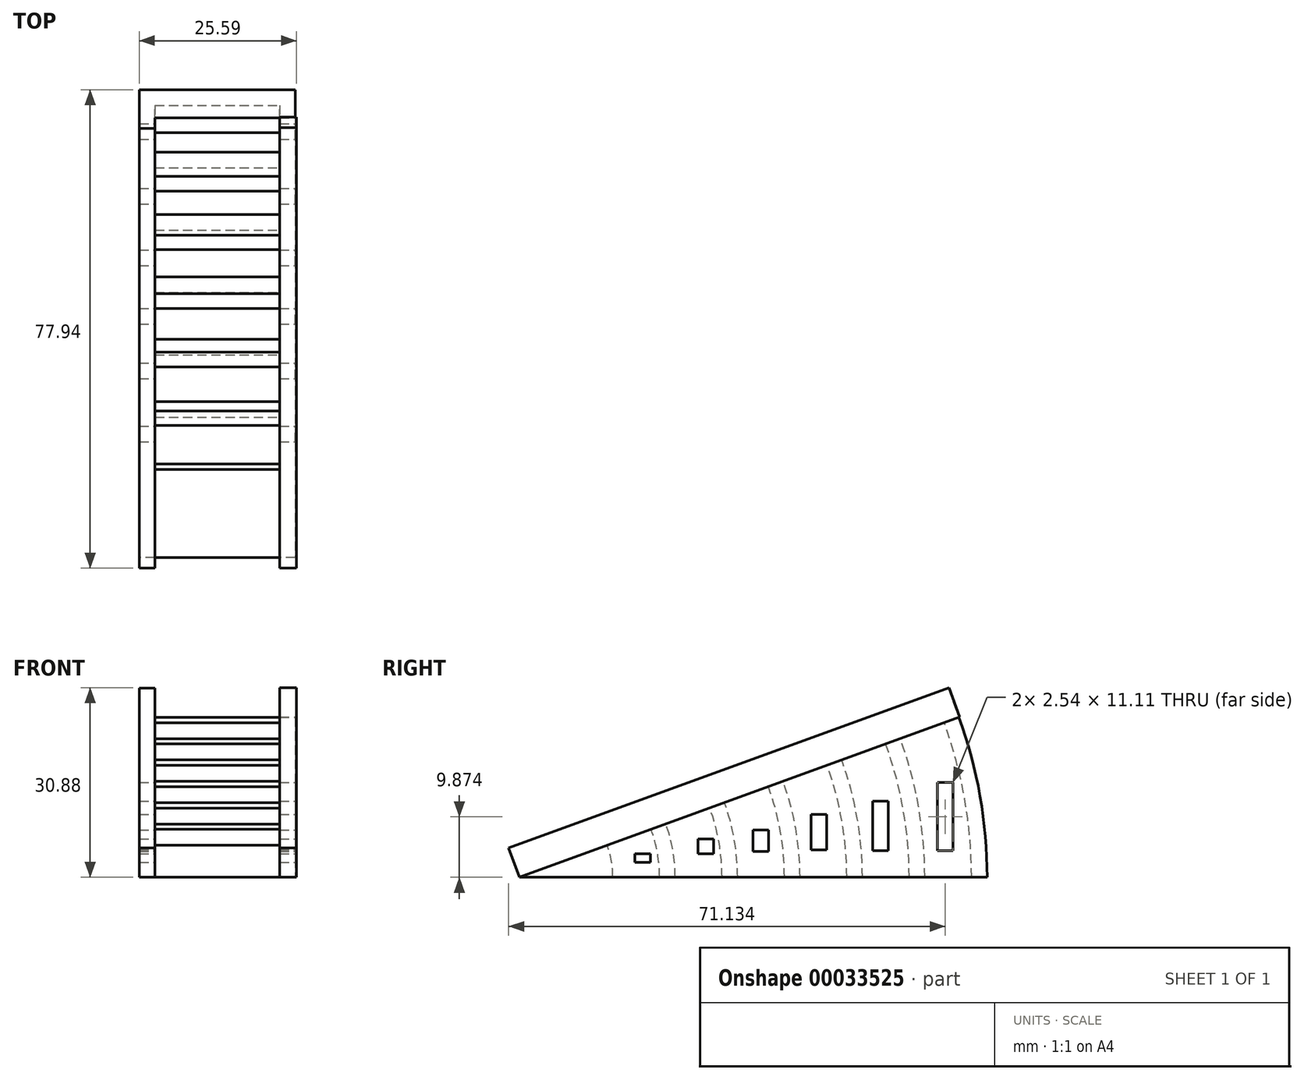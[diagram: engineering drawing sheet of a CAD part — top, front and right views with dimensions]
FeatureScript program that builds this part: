
annotation { "Feature Type Name" : "Feature", "Feature Type Description" : "" }
export const myFeature = defineFeature(function(context is Context, id is Id, definition is map)
    precondition{}
    {
        {
            var Q0;
            Q0=qCreatedBy(makeId("Top.planeOp"),FACE);
            var sketch = newSketch(context, id + "F0", { "sketchPlane" : qUnion([Q0])});
            skLineSegment(sketch, "E0", {"start": v(-12.56, 0) * mm, "end": v(-12.56, 76.2) * mm});
            skLineSegment(sketch, "E1", {"start": v(-12.56, 76.2) * mm, "end": v(12.84, 76.2) * mm});
            skLineSegment(sketch, "E2", {"start": v(12.84, 76.2) * mm, "end": v(12.84, 0) * mm});
            skLineSegment(sketch, "E3", {"start": v(12.84, 0) * mm, "end": v(-12.56, 0) * mm});
            skLineSegment(sketch, "E4.bottom", {"start": v(-10.02, 73.66) * mm, "end": v(10.3, 73.66) * mm});
            skLineSegment(sketch, "E4.top", {"start": v(-10.02, 66.04) * mm, "end": v(10.3, 66.04) * mm});
            skLineSegment(sketch, "E4.left", {"start": v(-10.02, 73.66) * mm, "end": v(-10.02, 66.04) * mm});
            skLineSegment(sketch, "E4.right", {"start": v(10.3, 73.66) * mm, "end": v(10.3, 66.04) * mm});
            skLineSegment(sketch, "E5.bottom", {"start": v(-10.02, 63.5) * mm, "end": v(10.3, 63.5) * mm});
            skLineSegment(sketch, "E5.top", {"start": v(-10.02, 55.88) * mm, "end": v(10.3, 55.88) * mm});
            skLineSegment(sketch, "E5.left", {"start": v(-10.02, 63.5) * mm, "end": v(-10.02, 55.88) * mm});
            skLineSegment(sketch, "E5.right", {"start": v(10.3, 63.5) * mm, "end": v(10.3, 55.88) * mm});
            skLineSegment(sketch, "E6.bottom", {"start": v(-10.02, 53.34) * mm, "end": v(10.3, 53.34) * mm});
            skLineSegment(sketch, "E6.top", {"start": v(-10.02, 45.72) * mm, "end": v(10.3, 45.72) * mm});
            skLineSegment(sketch, "E6.left", {"start": v(-10.02, 53.34) * mm, "end": v(-10.02, 45.72) * mm});
            skLineSegment(sketch, "E6.right", {"start": v(10.3, 53.34) * mm, "end": v(10.3, 45.72) * mm});
            skLineSegment(sketch, "E7.bottom", {"start": v(-10.02, 43.18) * mm, "end": v(10.3, 43.18) * mm});
            skLineSegment(sketch, "E7.top", {"start": v(-10.02, 35.56) * mm, "end": v(10.3, 35.56) * mm});
            skLineSegment(sketch, "E7.left", {"start": v(-10.02, 43.18) * mm, "end": v(-10.02, 35.56) * mm});
            skLineSegment(sketch, "E7.right", {"start": v(10.3, 43.18) * mm, "end": v(10.3, 35.56) * mm});
            skLineSegment(sketch, "E8.bottom", {"start": v(-10.02, 33.02) * mm, "end": v(10.3, 33.02) * mm});
            skLineSegment(sketch, "E8.top", {"start": v(-10.02, 25.4) * mm, "end": v(10.3, 25.4) * mm});
            skLineSegment(sketch, "E8.left", {"start": v(-10.02, 33.02) * mm, "end": v(-10.02, 25.4) * mm});
            skLineSegment(sketch, "E8.right", {"start": v(10.3, 33.02) * mm, "end": v(10.3, 25.4) * mm});
            skLineSegment(sketch, "E9.bottom", {"start": v(-10.02, 22.86) * mm, "end": v(10.3, 22.86) * mm});
            skLineSegment(sketch, "E9.top", {"start": v(-10.02, 15.24) * mm, "end": v(10.3, 15.24) * mm});
            skLineSegment(sketch, "E9.left", {"start": v(-10.02, 22.86) * mm, "end": v(-10.02, 15.24) * mm});
            skLineSegment(sketch, "E9.right", {"start": v(10.3, 22.86) * mm, "end": v(10.3, 15.24) * mm});
            skSolve(sketch);
        }
        {
            var Q0;
            Q0 = qSketchRegion(id + "F0", true);
            var Q1;
            Q1=sQuery(id+"F0.wireOp",EDGE,"E3");
            revolve(context, id + "F1", {"entities" : qUnion([Q0]), "axis" : qUnion([Q1]), "revolveType" : RevolveType.ONE_DIRECTION, "oppositeDirection" : true, "angle" : 20 * degree});
        }
        {
            var Q0;
            Q0=makeQuery(id+"F1.opRevolve","CAP_FACE",FACE,{"disambiguationData":[OSD([sQuery(id+"F0.wireOp",EDGE,"E0"),sQuery(id+"F0.wireOp",EDGE,"E1"),sQuery(id+"F0.wireOp",EDGE,"E2"),sQuery(id+"F0.wireOp",EDGE,"E3"),sQuery(id+"F0.wireOp",EDGE,"E4.bottom"),sQuery(id+"F0.wireOp",EDGE,"E4.top"),sQuery(id+"F0.wireOp",EDGE,"E4.left"),sQuery(id+"F0.wireOp",EDGE,"E4.right"),sQuery(id+"F0.wireOp",EDGE,"E5.bottom"),sQuery(id+"F0.wireOp",EDGE,"E5.top"),sQuery(id+"F0.wireOp",EDGE,"E5.left"),sQuery(id+"F0.wireOp",EDGE,"E5.right"),sQuery(id+"F0.wireOp",EDGE,"E6.bottom"),sQuery(id+"F0.wireOp",EDGE,"E6.top"),sQuery(id+"F0.wireOp",EDGE,"E6.left"),sQuery(id+"F0.wireOp",EDGE,"E6.right"),sQuery(id+"F0.wireOp",EDGE,"E7.bottom"),sQuery(id+"F0.wireOp",EDGE,"E7.top"),sQuery(id+"F0.wireOp",EDGE,"E7.left"),sQuery(id+"F0.wireOp",EDGE,"E7.right"),sQuery(id+"F0.wireOp",EDGE,"E8.bottom"),sQuery(id+"F0.wireOp",EDGE,"E8.top"),sQuery(id+"F0.wireOp",EDGE,"E8.left"),sQuery(id+"F0.wireOp",EDGE,"E8.right"),sQuery(id+"F0.wireOp",EDGE,"E9.bottom"),sQuery(id+"F0.wireOp",EDGE,"E9.top"),sQuery(id+"F0.wireOp",EDGE,"E9.left"),sQuery(id+"F0.wireOp",EDGE,"E9.right")])],"isStart":false});
            var sketch = newSketch(context, id + "F2", { "sketchPlane" : qUnion([Q0])});
            skLineSegment(sketch, "E10.bottom", {"start": v(-12.56, 76.2) * mm, "end": v(-10.02, 76.2) * mm});
            skLineSegment(sketch, "E10.top", {"start": v(-12.56, 0) * mm, "end": v(-10.02, 0) * mm});
            skLineSegment(sketch, "E10.left", {"start": v(-12.56, 76.2) * mm, "end": v(-12.56, 0) * mm});
            skLineSegment(sketch, "E10.right", {"start": v(-10.02, 76.2) * mm, "end": v(-10.02, 0) * mm});
            skLineSegment(sketch, "E11.bottom", {"start": v(10.33, 76.34) * mm, "end": v(13.03, 76.34) * mm});
            skLineSegment(sketch, "E11.top", {"start": v(10.33, 0) * mm, "end": v(13.03, 0) * mm});
            skLineSegment(sketch, "E11.left", {"start": v(10.33, 76.34) * mm, "end": v(10.33, 0) * mm});
            skLineSegment(sketch, "E11.right", {"start": v(13.03, 76.34) * mm, "end": v(13.03, 0) * mm});
            skSolve(sketch);
        }
        {
            var Q0;
            Q0 = qSketchRegion(id + "F2", true);
            var Q1;
            Q1 = qConstructionFilter(qBodyType(qCreatedBy(id + "F2" ,EDGE), BodyType.WIRE), ConstructionObject.NO);
            extrude(context, id + "F3", {"entities" : qUnion([Q0]), "operationType" : NewBodyOperationType.ADD, "surfaceEntities" : qUnion([Q1]), "depth" : 5.08 * mm});
        }
        {
            var Q0;
            Q0=makeQuery(id+"F1.opRevolve","SWEPT_FACE",FACE,{"disambiguationData":[OSD([sQuery(id+"F0.wireOp",EDGE,"E2")])]});
            var sketch = newSketch(context, id + "F4", { "sketchPlane" : qUnion([Q0])});
            skLineSegment(sketch, "E12.bottom", {"start": v(68.12, 15.43) * mm, "end": v(70.66, 15.43) * mm});
            skLineSegment(sketch, "E12.top", {"start": v(68.12, 4.32) * mm, "end": v(70.66, 4.32) * mm});
            skLineSegment(sketch, "E12.left", {"start": v(68.12, 15.43) * mm, "end": v(68.12, 4.32) * mm});
            skLineSegment(sketch, "E12.right", {"start": v(70.66, 15.43) * mm, "end": v(70.66, 4.32) * mm});
            skPoint(sketch, "E13.oppositeSnap0", {"position": v(69.4, 4.32) * mm});
            skLineSegment(sketch, "E13.bottom", {"start": v(57.56, 12.41) * mm, "end": v(60.1, 12.41) * mm});
            skLineSegment(sketch, "E13.top", {"start": v(57.56, 4.32) * mm, "end": v(60.1, 4.32) * mm});
            skLineSegment(sketch, "E13.left", {"start": v(57.56, 12.41) * mm, "end": v(57.56, 4.32) * mm});
            skLineSegment(sketch, "E13.right", {"start": v(60.1, 12.41) * mm, "end": v(60.1, 4.32) * mm});
            skLineSegment(sketch, "E14.bottom", {"start": v(47.55, 10.24) * mm, "end": v(50.09, 10.24) * mm});
            skLineSegment(sketch, "E14.top", {"start": v(47.55, 4.44) * mm, "end": v(50.09, 4.44) * mm});
            skLineSegment(sketch, "E14.left", {"start": v(47.55, 10.24) * mm, "end": v(47.55, 4.44) * mm});
            skLineSegment(sketch, "E14.right", {"start": v(50.09, 10.24) * mm, "end": v(50.09, 4.44) * mm});
            skLineSegment(sketch, "E15.bottom", {"start": v(38.04, 7.72) * mm, "end": v(40.58, 7.72) * mm});
            skLineSegment(sketch, "E15.top", {"start": v(38.04, 4.2) * mm, "end": v(40.58, 4.2) * mm});
            skLineSegment(sketch, "E15.left", {"start": v(38.04, 7.72) * mm, "end": v(38.04, 4.2) * mm});
            skLineSegment(sketch, "E15.right", {"start": v(40.58, 7.72) * mm, "end": v(40.58, 4.2) * mm});
            skLineSegment(sketch, "E16.bottom", {"start": v(29.1, 6.26) * mm, "end": v(31.63, 6.26) * mm});
            skLineSegment(sketch, "E16.top", {"start": v(29.1, 3.84) * mm, "end": v(31.63, 3.84) * mm});
            skLineSegment(sketch, "E16.left", {"start": v(29.1, 6.26) * mm, "end": v(29.1, 3.84) * mm});
            skLineSegment(sketch, "E16.right", {"start": v(31.63, 6.26) * mm, "end": v(31.63, 3.84) * mm});
            skLineSegment(sketch, "E17.bottom", {"start": v(18.81, 3.84) * mm, "end": v(21.35, 3.84) * mm});
            skLineSegment(sketch, "E17.top", {"start": v(18.81, 2.44) * mm, "end": v(21.35, 2.44) * mm});
            skLineSegment(sketch, "E17.left", {"start": v(18.81, 3.84) * mm, "end": v(18.81, 2.44) * mm});
            skLineSegment(sketch, "E17.right", {"start": v(21.35, 3.84) * mm, "end": v(21.35, 2.44) * mm});
            skSolve(sketch);
        }
        {
            var Q0;
            Q0 = qSketchRegion(id + "F4", true);
            extrude(context, id + "F5", {"entities" : qUnion([Q0]), "operationType" : NewBodyOperationType.REMOVE, "endBound" : BoundingType.THROUGH_ALL, "oppositeDirection" : true, "depth" : 25.4 * mm});
        }
    });
